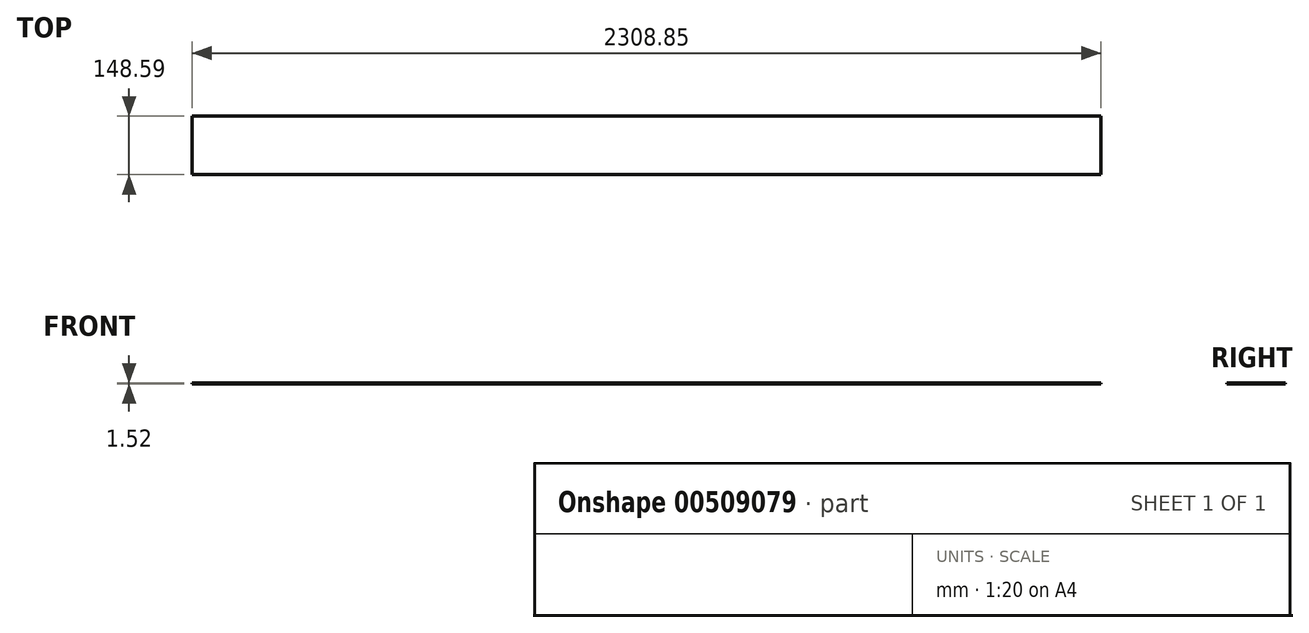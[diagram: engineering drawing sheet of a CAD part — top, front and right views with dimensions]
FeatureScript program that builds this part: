
annotation { "Feature Type Name" : "Feature", "Feature Type Description" : "" }
export const myFeature = defineFeature(function(context is Context, id is Id, definition is map)
    precondition{}
    {
        {
            var Q0;
            Q0=qCreatedBy(makeId("Right.planeOp"),FACE);
            var sketch = newSketch(context, id + "F0", { "sketchPlane" : qUnion([Q0])});
            skLineSegment(sketch, "E0", {"start": v(-72.51, 32.91) * mm, "end": v(76.08, 32.91) * mm});
            skLineSegment(sketch, "E1", {"start": v(76.08, 32.91) * mm, "end": v(76.08, 31.4) * mm});
            skLineSegment(sketch, "E2", {"start": v(76.08, 31.4) * mm, "end": v(-72.51, 31.4) * mm});
            skLineSegment(sketch, "E3", {"start": v(-72.51, 32.91) * mm, "end": v(-72.51, 31.4) * mm});
            skSolve(sketch);
        }
        {
            var Q0;
            Q0 = qSketchRegion(id + "F0", true);
            extrude(context, id + "F1", {"entities" : qUnion([Q0]), "depth" : 2308.85 * mm});
        }
    });
